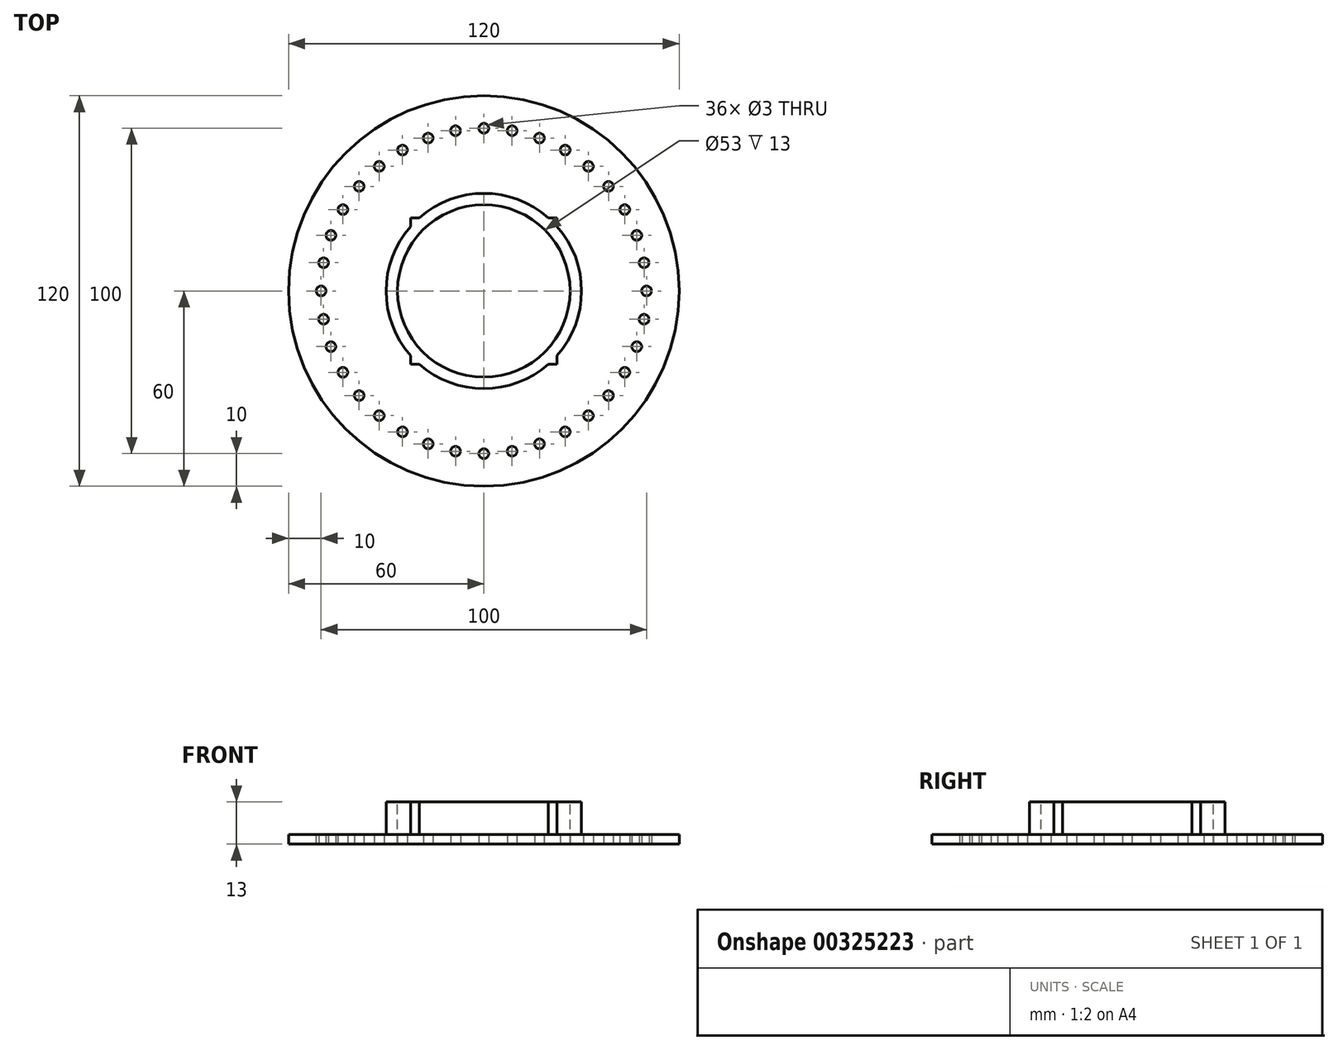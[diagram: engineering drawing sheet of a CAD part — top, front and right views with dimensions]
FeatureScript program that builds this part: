
annotation { "Feature Type Name" : "Feature", "Feature Type Description" : "" }
export const myFeature = defineFeature(function(context is Context, id is Id, definition is map)
    precondition{}
    {
        {
            var Q0;
            Q0=qCreatedBy(makeId("Top.planeOp"),FACE);
            var sketch = newSketch(context, id + "F0", { "sketchPlane" : qUnion([Q0])});
            skCircle(sketch, "E0", {"center": v(0, 0) * mm, "radius": 60 * mm});
            skCircle(sketch, "E1", {"center": v(0, -50) * mm, "radius": 1.5 * mm});
            skCircle(sketch, "E2.1.0", {"center": v(8.68, -49.24) * mm, "radius": 1.5 * mm});
            skCircle(sketch, "E2.2.0", {"center": v(17.1, -46.98) * mm, "radius": 1.5 * mm});
            skCircle(sketch, "E2.3.0", {"center": v(25, -43.3) * mm, "radius": 1.5 * mm});
            skCircle(sketch, "E2.4.0", {"center": v(32.14, -38.3) * mm, "radius": 1.5 * mm});
            skCircle(sketch, "E2.5.0", {"center": v(38.3, -32.14) * mm, "radius": 1.5 * mm});
            skCircle(sketch, "E2.6.0", {"center": v(43.3, -25) * mm, "radius": 1.5 * mm});
            skCircle(sketch, "E2.7.0", {"center": v(46.98, -17.1) * mm, "radius": 1.5 * mm});
            skCircle(sketch, "E2.8.0", {"center": v(49.24, -8.68) * mm, "radius": 1.5 * mm});
            skCircle(sketch, "E2.9.0", {"center": v(50, 0) * mm, "radius": 1.5 * mm});
            skCircle(sketch, "E2.10.0", {"center": v(49.24, 8.68) * mm, "radius": 1.5 * mm});
            skCircle(sketch, "E2.11.0", {"center": v(46.98, 17.1) * mm, "radius": 1.5 * mm});
            skCircle(sketch, "E2.12.0", {"center": v(43.3, 25) * mm, "radius": 1.5 * mm});
            skCircle(sketch, "E2.13.0", {"center": v(38.3, 32.14) * mm, "radius": 1.5 * mm});
            skCircle(sketch, "E2.14.0", {"center": v(32.14, 38.3) * mm, "radius": 1.5 * mm});
            skCircle(sketch, "E2.15.0", {"center": v(25, 43.3) * mm, "radius": 1.5 * mm});
            skCircle(sketch, "E2.16.0", {"center": v(17.1, 46.98) * mm, "radius": 1.5 * mm});
            skCircle(sketch, "E2.17.0", {"center": v(8.68, 49.24) * mm, "radius": 1.5 * mm});
            skCircle(sketch, "E2.18.0", {"center": v(0, 50) * mm, "radius": 1.5 * mm});
            skCircle(sketch, "E2.19.0", {"center": v(-8.68, 49.24) * mm, "radius": 1.5 * mm});
            skCircle(sketch, "E2.20.0", {"center": v(-17.1, 46.98) * mm, "radius": 1.5 * mm});
            skCircle(sketch, "E2.21.0", {"center": v(-25, 43.3) * mm, "radius": 1.5 * mm});
            skCircle(sketch, "E2.22.0", {"center": v(-32.14, 38.3) * mm, "radius": 1.5 * mm});
            skCircle(sketch, "E2.23.0", {"center": v(-38.3, 32.14) * mm, "radius": 1.5 * mm});
            skCircle(sketch, "E2.24.0", {"center": v(-43.3, 25) * mm, "radius": 1.5 * mm});
            skCircle(sketch, "E2.25.0", {"center": v(-46.98, 17.1) * mm, "radius": 1.5 * mm});
            skCircle(sketch, "E2.26.0", {"center": v(-49.24, 8.68) * mm, "radius": 1.5 * mm});
            skCircle(sketch, "E2.27.0", {"center": v(-50, 0) * mm, "radius": 1.5 * mm});
            skCircle(sketch, "E2.28.0", {"center": v(-49.24, -8.68) * mm, "radius": 1.5 * mm});
            skCircle(sketch, "E2.29.0", {"center": v(-46.98, -17.1) * mm, "radius": 1.5 * mm});
            skCircle(sketch, "E2.30.0", {"center": v(-43.3, -25) * mm, "radius": 1.5 * mm});
            skCircle(sketch, "E2.31.0", {"center": v(-38.3, -32.14) * mm, "radius": 1.5 * mm});
            skCircle(sketch, "E2.32.0", {"center": v(-32.14, -38.3) * mm, "radius": 1.5 * mm});
            skCircle(sketch, "E2.33.0", {"center": v(-25, -43.3) * mm, "radius": 1.5 * mm});
            skCircle(sketch, "E2.34.0", {"center": v(-17.1, -46.98) * mm, "radius": 1.5 * mm});
            skCircle(sketch, "E2.35.0", {"center": v(-8.68, -49.24) * mm, "radius": 1.5 * mm});
            skLineSegment(sketch, "E2.anchor1", {"start": v(0, 0) * mm, "end": v(0, -50) * mm, "construction": true});
            skLineSegment(sketch, "E2.anchor2", {"start": v(0, 0) * mm, "end": v(-8.68, -49.24) * mm, "construction": true});
            skSolve(sketch);
        }
        {
            var Q0;
            Q0=makeQuery(id+"F0.imprint","IMPRINT",FACE,{"disambiguationData":[TD([[makeQuery(id+"F0.imprint","IMPRINT",EDGE,{"derivedFrom":sQuery(id+"F0.wireOp",EDGE,"E1")}),-1.0]])]});
            extrude(context, id + "F1", {"entities" : qUnion([Q0]), "depth" : 3 * mm});
        }
        {
            var Q0;
            Q0=makeQuery(id+"F1.opExtrude","CAP_FACE",FACE,{"disambiguationData":[OSD([sQuery(id+"F0.wireOp",EDGE,"E1"),sQuery(id+"F0.wireOp",EDGE,"E2.1.0"),sQuery(id+"F0.wireOp",EDGE,"E2.2.0"),sQuery(id+"F0.wireOp",EDGE,"E2.3.0"),sQuery(id+"F0.wireOp",EDGE,"E2.4.0"),sQuery(id+"F0.wireOp",EDGE,"E2.5.0"),sQuery(id+"F0.wireOp",EDGE,"E2.6.0"),sQuery(id+"F0.wireOp",EDGE,"E2.7.0"),sQuery(id+"F0.wireOp",EDGE,"E2.8.0"),sQuery(id+"F0.wireOp",EDGE,"E2.9.0"),sQuery(id+"F0.wireOp",EDGE,"E2.10.0"),sQuery(id+"F0.wireOp",EDGE,"E2.11.0"),sQuery(id+"F0.wireOp",EDGE,"E2.12.0"),sQuery(id+"F0.wireOp",EDGE,"E2.13.0"),sQuery(id+"F0.wireOp",EDGE,"E2.14.0"),sQuery(id+"F0.wireOp",EDGE,"E2.15.0"),sQuery(id+"F0.wireOp",EDGE,"E2.16.0"),sQuery(id+"F0.wireOp",EDGE,"E2.17.0"),sQuery(id+"F0.wireOp",EDGE,"E2.18.0"),sQuery(id+"F0.wireOp",EDGE,"E2.19.0"),sQuery(id+"F0.wireOp",EDGE,"E2.20.0"),sQuery(id+"F0.wireOp",EDGE,"E2.21.0"),sQuery(id+"F0.wireOp",EDGE,"E2.22.0"),sQuery(id+"F0.wireOp",EDGE,"E2.23.0"),sQuery(id+"F0.wireOp",EDGE,"E2.24.0"),sQuery(id+"F0.wireOp",EDGE,"E2.25.0"),sQuery(id+"F0.wireOp",EDGE,"E2.26.0"),sQuery(id+"F0.wireOp",EDGE,"E2.27.0"),sQuery(id+"F0.wireOp",EDGE,"E2.28.0"),sQuery(id+"F0.wireOp",EDGE,"E2.29.0"),sQuery(id+"F0.wireOp",EDGE,"E2.30.0"),sQuery(id+"F0.wireOp",EDGE,"E2.31.0"),sQuery(id+"F0.wireOp",EDGE,"E2.32.0"),sQuery(id+"F0.wireOp",EDGE,"E2.33.0"),sQuery(id+"F0.wireOp",EDGE,"E2.34.0"),sQuery(id+"F0.wireOp",EDGE,"E2.35.0"),sQuery(id+"F0.wireOp",EDGE,"E0")])],"isStart":false});
            var sketch = newSketch(context, id + "F2", { "sketchPlane" : qUnion([Q0])});
            skCircle(sketch, "E3", {"center": v(0, 0) * mm, "radius": 26.5 * mm});
            skSolve(sketch);
        }
        {
            var Q0;
            Q0=makeQuery(id+"F2.imprint","IMPRINT",FACE,{"disambiguationData":[TD([[makeQuery(id+"F2.imprint","IMPRINT",EDGE,{"derivedFrom":sQuery(id+"F2.wireOp",EDGE,"E3")}),1.0]])]});
            extrude(context, id + "F3", {"entities" : qUnion([Q0]), "operationType" : NewBodyOperationType.REMOVE, "oppositeDirection" : true, "depth" : 25 * mm});
        }
        {
            var Q0;
            Q0=makeQuery(id+"F1.opExtrude","CAP_FACE",FACE,{"disambiguationData":[OSD([sQuery(id+"F0.wireOp",EDGE,"E1"),sQuery(id+"F0.wireOp",EDGE,"E2.1.0"),sQuery(id+"F0.wireOp",EDGE,"E2.2.0"),sQuery(id+"F0.wireOp",EDGE,"E2.3.0"),sQuery(id+"F0.wireOp",EDGE,"E2.4.0"),sQuery(id+"F0.wireOp",EDGE,"E2.5.0"),sQuery(id+"F0.wireOp",EDGE,"E2.6.0"),sQuery(id+"F0.wireOp",EDGE,"E2.7.0"),sQuery(id+"F0.wireOp",EDGE,"E2.8.0"),sQuery(id+"F0.wireOp",EDGE,"E2.9.0"),sQuery(id+"F0.wireOp",EDGE,"E2.10.0"),sQuery(id+"F0.wireOp",EDGE,"E2.11.0"),sQuery(id+"F0.wireOp",EDGE,"E2.12.0"),sQuery(id+"F0.wireOp",EDGE,"E2.13.0"),sQuery(id+"F0.wireOp",EDGE,"E2.14.0"),sQuery(id+"F0.wireOp",EDGE,"E2.15.0"),sQuery(id+"F0.wireOp",EDGE,"E2.16.0"),sQuery(id+"F0.wireOp",EDGE,"E2.17.0"),sQuery(id+"F0.wireOp",EDGE,"E2.18.0"),sQuery(id+"F0.wireOp",EDGE,"E2.19.0"),sQuery(id+"F0.wireOp",EDGE,"E2.20.0"),sQuery(id+"F0.wireOp",EDGE,"E2.21.0"),sQuery(id+"F0.wireOp",EDGE,"E2.22.0"),sQuery(id+"F0.wireOp",EDGE,"E2.23.0"),sQuery(id+"F0.wireOp",EDGE,"E2.24.0"),sQuery(id+"F0.wireOp",EDGE,"E2.25.0"),sQuery(id+"F0.wireOp",EDGE,"E2.26.0"),sQuery(id+"F0.wireOp",EDGE,"E2.27.0"),sQuery(id+"F0.wireOp",EDGE,"E2.28.0"),sQuery(id+"F0.wireOp",EDGE,"E2.29.0"),sQuery(id+"F0.wireOp",EDGE,"E2.30.0"),sQuery(id+"F0.wireOp",EDGE,"E2.31.0"),sQuery(id+"F0.wireOp",EDGE,"E2.32.0"),sQuery(id+"F0.wireOp",EDGE,"E2.33.0"),sQuery(id+"F0.wireOp",EDGE,"E2.34.0"),sQuery(id+"F0.wireOp",EDGE,"E2.35.0"),sQuery(id+"F0.wireOp",EDGE,"E0")])],"isStart":false});
            var sketch = newSketch(context, id + "F4", { "sketchPlane" : qUnion([Q0])});
            skCircle(sketch, "E4", {"center": v(0, 0) * mm, "radius": 30 * mm});
            skSolve(sketch);
        }
        {
            var Q0;
            Q0=makeQuery(id+"F4.imprint","IMPRINT",FACE,{"disambiguationData":[TD([[makeQuery(id+"F4.imprint","IMPRINT",EDGE,{"derivedFrom":sQuery(id+"F4.wireOp",EDGE,"E4")}),1.0]])]});
            extrude(context, id + "F5", {"entities" : qUnion([Q0]), "operationType" : NewBodyOperationType.ADD, "depth" : 10 * mm});
        }
        {
            var Q0;
            Q0=makeQuery(id+"F1.opExtrude","CAP_FACE",FACE,{"disambiguationData":[OSD([sQuery(id+"F0.wireOp",EDGE,"E1"),sQuery(id+"F0.wireOp",EDGE,"E2.1.0"),sQuery(id+"F0.wireOp",EDGE,"E2.2.0"),sQuery(id+"F0.wireOp",EDGE,"E2.3.0"),sQuery(id+"F0.wireOp",EDGE,"E2.4.0"),sQuery(id+"F0.wireOp",EDGE,"E2.5.0"),sQuery(id+"F0.wireOp",EDGE,"E2.6.0"),sQuery(id+"F0.wireOp",EDGE,"E2.7.0"),sQuery(id+"F0.wireOp",EDGE,"E2.8.0"),sQuery(id+"F0.wireOp",EDGE,"E2.9.0"),sQuery(id+"F0.wireOp",EDGE,"E2.10.0"),sQuery(id+"F0.wireOp",EDGE,"E2.11.0"),sQuery(id+"F0.wireOp",EDGE,"E2.12.0"),sQuery(id+"F0.wireOp",EDGE,"E2.13.0"),sQuery(id+"F0.wireOp",EDGE,"E2.14.0"),sQuery(id+"F0.wireOp",EDGE,"E2.15.0"),sQuery(id+"F0.wireOp",EDGE,"E2.16.0"),sQuery(id+"F0.wireOp",EDGE,"E2.17.0"),sQuery(id+"F0.wireOp",EDGE,"E2.18.0"),sQuery(id+"F0.wireOp",EDGE,"E2.19.0"),sQuery(id+"F0.wireOp",EDGE,"E2.20.0"),sQuery(id+"F0.wireOp",EDGE,"E2.21.0"),sQuery(id+"F0.wireOp",EDGE,"E2.22.0"),sQuery(id+"F0.wireOp",EDGE,"E2.23.0"),sQuery(id+"F0.wireOp",EDGE,"E2.24.0"),sQuery(id+"F0.wireOp",EDGE,"E2.25.0"),sQuery(id+"F0.wireOp",EDGE,"E2.26.0"),sQuery(id+"F0.wireOp",EDGE,"E2.27.0"),sQuery(id+"F0.wireOp",EDGE,"E2.28.0"),sQuery(id+"F0.wireOp",EDGE,"E2.29.0"),sQuery(id+"F0.wireOp",EDGE,"E2.30.0"),sQuery(id+"F0.wireOp",EDGE,"E2.31.0"),sQuery(id+"F0.wireOp",EDGE,"E2.32.0"),sQuery(id+"F0.wireOp",EDGE,"E2.33.0"),sQuery(id+"F0.wireOp",EDGE,"E2.34.0"),sQuery(id+"F0.wireOp",EDGE,"E2.35.0"),sQuery(id+"F0.wireOp",EDGE,"E0")])],"isStart":false});
            var sketch = newSketch(context, id + "F6", { "sketchPlane" : qUnion([Q0])});
            skLineSegment(sketch, "E5.bottom", {"start": v(22.5, 22.5) * mm, "end": v(-22.5, 22.5) * mm});
            skLineSegment(sketch, "E5.top", {"start": v(22.5, -22.5) * mm, "end": v(-22.5, -22.5) * mm});
            skLineSegment(sketch, "E5.left", {"start": v(22.5, 22.5) * mm, "end": v(22.5, -22.5) * mm});
            skLineSegment(sketch, "E5.right", {"start": v(-22.5, 22.5) * mm, "end": v(-22.5, -22.5) * mm});
            skPoint(sketch, "E5.middle", {"position": v(0, 0) * mm});
            skSolve(sketch);
        }
        {
            var Q0;
            {var subQ0=sQuery(id+"F6.wireOp",EDGE,"E5.right");var subQ1=sQuery(id+"F6.wireOp",EDGE,"E5.top");var subQ2=makeQuery(id+"F6.imprint","INTERSECT",VERTEX,{"derivedFrom":[subQ1,subQ0]});Q0=makeQuery(id+"F6.imprint","IMPRINT",FACE,{"disambiguationData":[TD([[makeQuery(id+"F6.imprint","IMPRINT",EDGE,{"disambiguationData":[TD([[subQ2,1.0]])],"derivedFrom":subQ1}),-1.0]])]});}
            var Q1;
            {var subQ0=sQuery(id+"F6.wireOp",EDGE,"E5.left");var subQ1=sQuery(id+"F6.wireOp",EDGE,"E5.top");var subQ2=makeQuery(id+"F6.imprint","INTERSECT",VERTEX,{"derivedFrom":[subQ1,subQ0]});Q1=makeQuery(id+"F6.imprint","IMPRINT",FACE,{"disambiguationData":[TD([[makeQuery(id+"F6.imprint","IMPRINT",EDGE,{"disambiguationData":[TD([[subQ2,-1.0]])],"derivedFrom":subQ1}),-1.0]])]});}
            var Q2;
            {var subQ0=sQuery(id+"F6.wireOp",EDGE,"E5.left");var subQ1=sQuery(id+"F6.wireOp",EDGE,"E5.bottom");var subQ2=makeQuery(id+"F6.imprint","INTERSECT",VERTEX,{"derivedFrom":[subQ1,subQ0]});Q2=makeQuery(id+"F6.imprint","IMPRINT",FACE,{"disambiguationData":[TD([[makeQuery(id+"F6.imprint","IMPRINT",EDGE,{"disambiguationData":[TD([[subQ2,-1.0]])],"derivedFrom":subQ1}),1.0]])]});}
            var Q3;
            {var subQ0=sQuery(id+"F6.wireOp",EDGE,"E5.right");var subQ1=sQuery(id+"F6.wireOp",EDGE,"E5.bottom");var subQ2=makeQuery(id+"F6.imprint","INTERSECT",VERTEX,{"derivedFrom":[subQ1,subQ0]});Q3=makeQuery(id+"F6.imprint","IMPRINT",FACE,{"disambiguationData":[TD([[makeQuery(id+"F6.imprint","IMPRINT",EDGE,{"disambiguationData":[TD([[subQ2,1.0]])],"derivedFrom":subQ1}),1.0]])]});}
            extrude(context, id + "F7", {"entities" : qUnion([Q0, Q1, Q2, Q3]), "operationType" : NewBodyOperationType.ADD, "depth" : 10 * mm});
        }
    });
